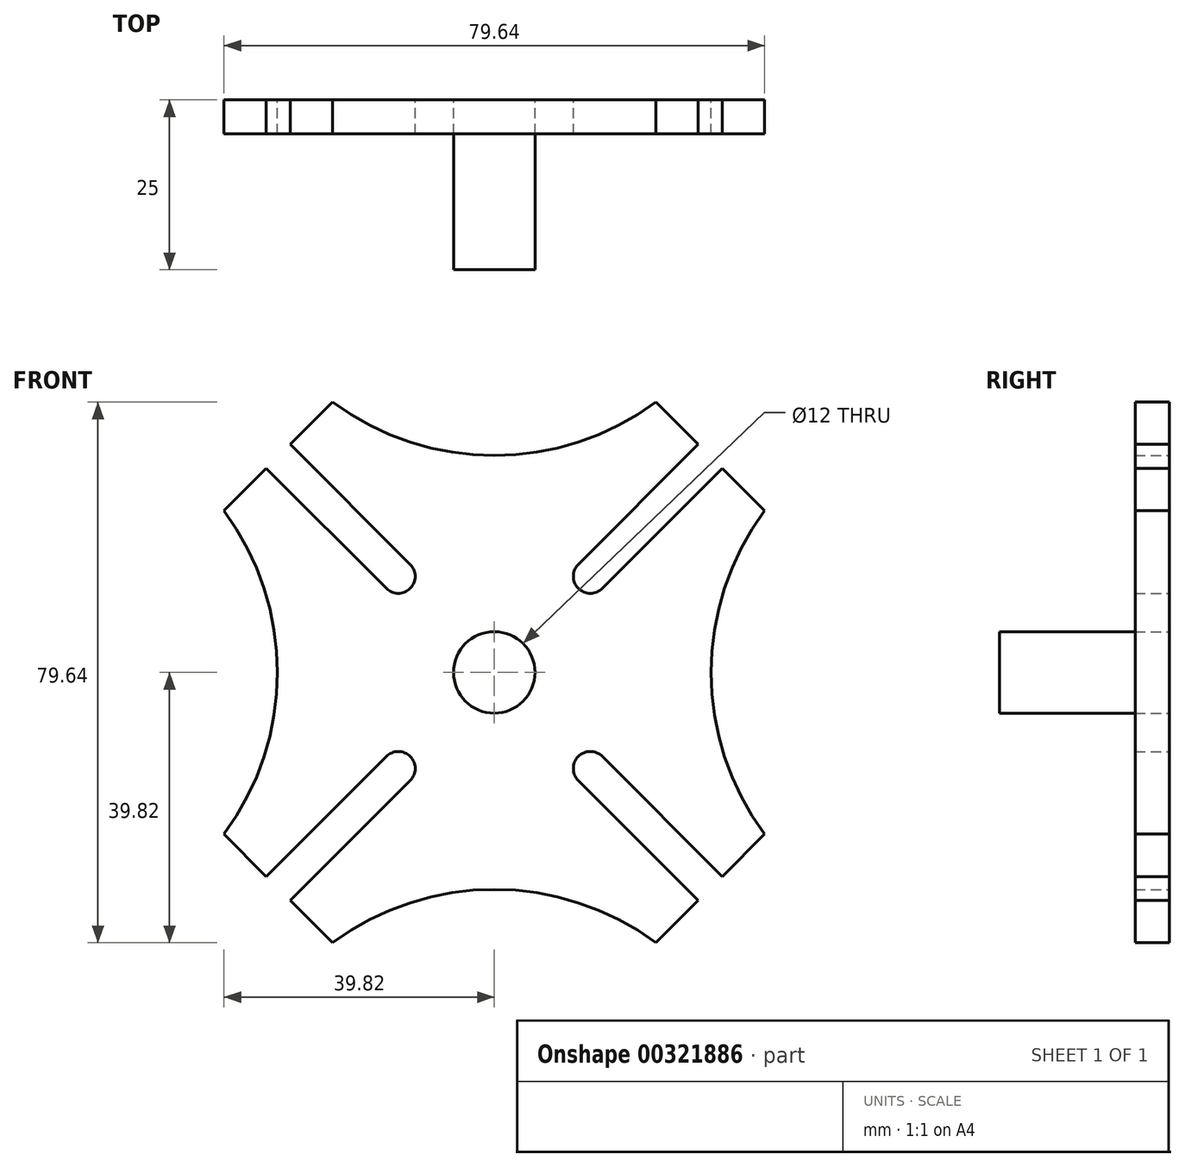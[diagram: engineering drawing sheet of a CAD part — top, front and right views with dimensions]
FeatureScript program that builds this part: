
annotation { "Feature Type Name" : "Feature", "Feature Type Description" : "" }
export const myFeature = defineFeature(function(context is Context, id is Id, definition is map)
    precondition{}
    {
        {
            var Q0;
            Q0=qCreatedBy(makeId("Front.planeOp"),FACE);
            var sketch = newSketch(context, id + "F0", { "sketchPlane" : qUnion([Q0])});
            skPoint(sketch, "E0.middle", {"position": v(0, 0) * mm});
            skArc(sketch, "E1", {"start": v(-23.82, 39.82) * mm, "mid": v(0, 31.96) * mm, "end": v(23.82, 39.82) * mm});
            skArc(sketch, "E2", {"start": v(39.82, 23.82) * mm, "mid": v(31.95, 0) * mm, "end": v(39.82, -23.82) * mm});
            skPoint(sketch, "E3.orphan", {"position": v(40, 40) * mm});
            skLineSegment(sketch, "E4", {"start": v(23.82, 39.82) * mm, "end": v(30.05, 33.6) * mm});
            skArc(sketch, "E5.MirrorCS", {"start": v(-39.82, 23.82) * mm, "mid": v(-31.95, 0) * mm, "end": v(-39.82, -23.82) * mm});
            skArc(sketch, "E6.MirrorCS", {"start": v(-23.82, -39.82) * mm, "mid": v(0, -31.96) * mm, "end": v(23.82, -39.82) * mm});
            skLineSegment(sketch, "E7", {"start": v(23.82, -39.82) * mm, "end": v(30.05, -33.6) * mm});
            skLineSegment(sketch, "E8", {"start": v(-39.82, 23.82) * mm, "end": v(-33.58, 30.06) * mm});
            skLineSegment(sketch, "E9", {"start": v(-39.82, -23.82) * mm, "end": v(-33.58, -30.06) * mm});
            skPoint(sketch, "E0.right.start.orphan", {"position": v(-40, 40) * mm});
            skPoint(sketch, "E10.trimOffspring.end.orphan", {"position": v(-40, -40) * mm});
            skPoint(sketch, "E11.trimOffspring.end.orphan", {"position": v(40, -40) * mm});
            skCircle(sketch, "E12", {"center": v(0, 0) * mm, "radius": 6 * mm});
            skLineSegment(sketch, "E13", {"start": v(0, 0) * mm, "end": v(53.2, 53.2) * mm, "construction": true});
            skLineSegment(sketch, "E14", {"start": v(0, 0) * mm, "end": v(-47.6, 47.6) * mm, "construction": true});
            skLineSegment(sketch, "E15", {"start": v(30.05, 33.6) * mm, "end": v(12.37, 15.91) * mm});
            skLineSegment(sketch, "E16", {"start": v(15.9, 12.38) * mm, "end": v(33.58, 30.06) * mm});
            skArc(sketch, "E17", {"start": v(12.37, 15.91) * mm, "mid": v(12.37, 12.38) * mm, "end": v(15.9, 12.38) * mm});
            skLineSegment(sketch, "E18.trimOffspring", {"start": v(33.58, 30.06) * mm, "end": v(39.82, 23.82) * mm});
            skLineSegment(sketch, "E19.MirrorCS", {"start": v(-30.05, 33.6) * mm, "end": v(-12.37, 15.91) * mm});
            skLineSegment(sketch, "E20.MirrorCS", {"start": v(-15.9, 12.38) * mm, "end": v(-33.58, 30.06) * mm});
            skArc(sketch, "E21.MirrorCS", {"start": v(-12.37, 15.91) * mm, "mid": v(-12.37, 12.38) * mm, "end": v(-15.9, 12.38) * mm});
            skLineSegment(sketch, "E22.MirrorCS", {"start": v(15.9, -12.38) * mm, "end": v(33.58, -30.06) * mm});
            skLineSegment(sketch, "E23.MirrorCS", {"start": v(30.05, -33.6) * mm, "end": v(12.37, -15.91) * mm});
            skArc(sketch, "E24.MirrorCS", {"start": v(12.37, -15.91) * mm, "mid": v(12.37, -12.38) * mm, "end": v(15.9, -12.38) * mm});
            skLineSegment(sketch, "E25.MirrorCS", {"start": v(-15.9, -12.38) * mm, "end": v(-33.58, -30.06) * mm});
            skLineSegment(sketch, "E26.MirrorCS", {"start": v(-30.05, -33.6) * mm, "end": v(-12.37, -15.91) * mm});
            skArc(sketch, "E27.MirrorCS", {"start": v(-12.37, -15.91) * mm, "mid": v(-12.37, -12.38) * mm, "end": v(-15.9, -12.38) * mm});
            skLineSegment(sketch, "E28.trimOffspring", {"start": v(-30.05, 33.6) * mm, "end": v(-23.82, 39.82) * mm});
            skLineSegment(sketch, "E29.trimOffspring", {"start": v(-30.05, -33.6) * mm, "end": v(-23.82, -39.82) * mm});
            skLineSegment(sketch, "E30.trimOffspring", {"start": v(33.58, -30.06) * mm, "end": v(39.82, -23.82) * mm});
            skSolve(sketch);
        }
        {
            var Q0;
            Q0=makeQuery(id+"F0.imprint","IMPRINT",FACE,{"disambiguationData":[TD([[makeQuery(id+"F0.imprint","IMPRINT",EDGE,{"derivedFrom":sQuery(id+"F0.wireOp",EDGE,"E1")}),-1.0]])]});
            extrude(context, id + "F1", {"entities" : qUnion([Q0]), "depth" : 5 * mm});
        }
        {
            var Q0;
            Q0=makeQuery(id+"F0.imprint","IMPRINT",FACE,{"disambiguationData":[TD([[makeQuery(id+"F0.imprint","IMPRINT",EDGE,{"derivedFrom":sQuery(id+"F0.wireOp",EDGE,"E12")}),1.0]])]});
            extrude(context, id + "F2", {"entities" : qUnion([Q0]), "depth" : 25 * mm});
        }
    });
